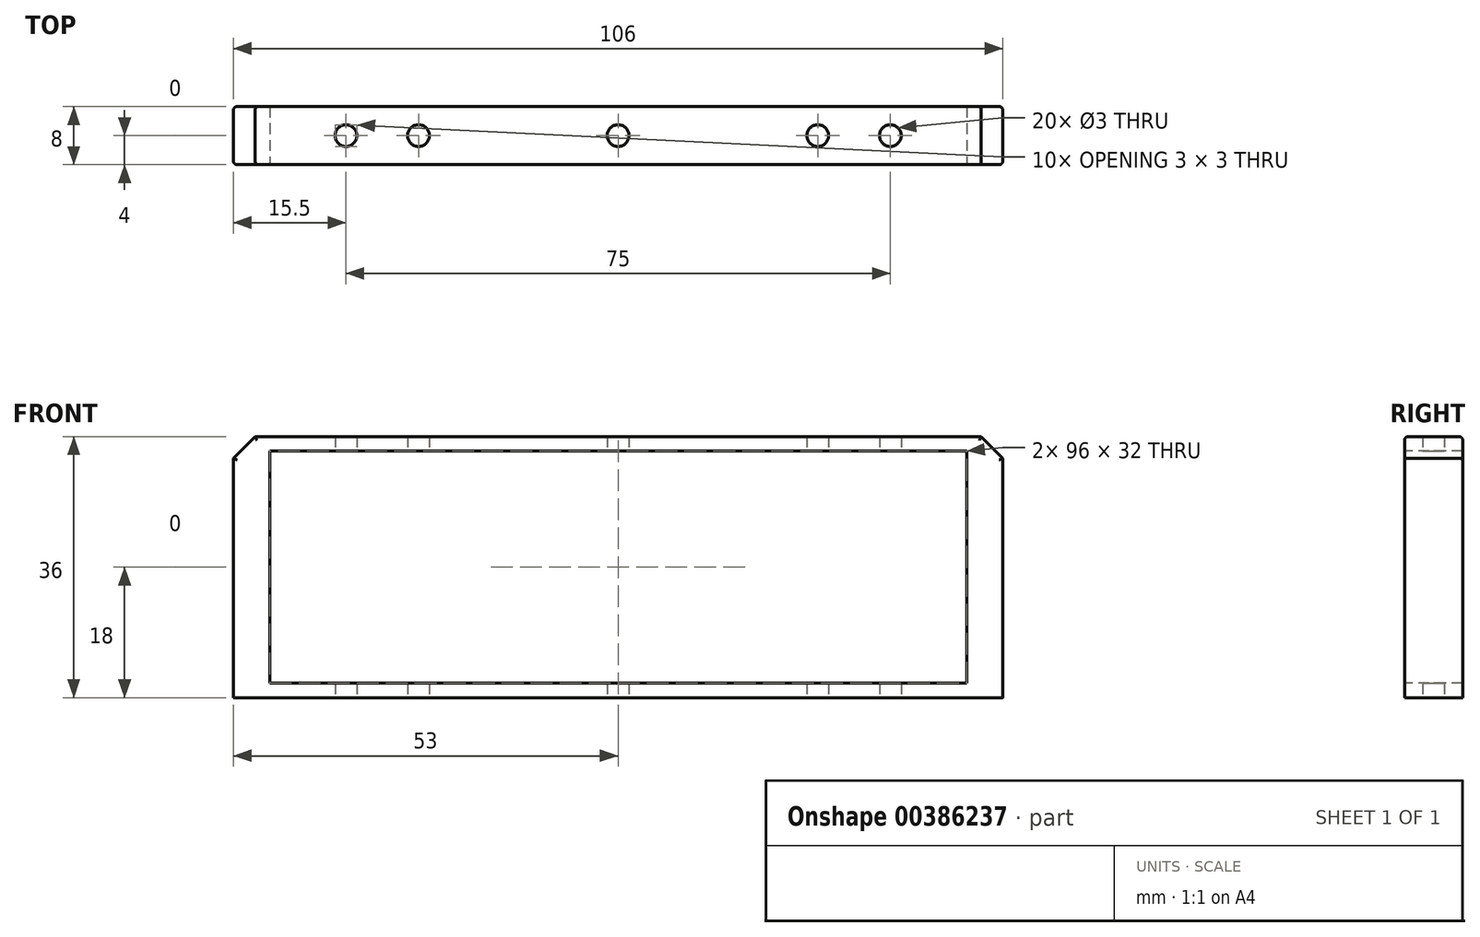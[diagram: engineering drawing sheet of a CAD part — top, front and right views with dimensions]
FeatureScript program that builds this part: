
annotation { "Feature Type Name" : "Feature", "Feature Type Description" : "" }
export const myFeature = defineFeature(function(context is Context, id is Id, definition is map)
    precondition{}
    {
        {
            assignVariable(context, id + "F0", {"name" : "height", "anyValue" : 36});
        }
        {
            var Q0;
            Q0=qCreatedBy(makeId("Top.planeOp"),FACE);
            var sketch = newSketch(context, id + "F1", { "sketchPlane" : qUnion([Q0])});
            skCircle(sketch, "E0", {"center": v(0, 0) * mm, "radius": 1.5 * mm});
            skCircle(sketch, "E1", {"center": v(37.5, 0) * mm, "radius": 1.5 * mm});
            skCircle(sketch, "E2", {"center": v(-37.5, 0) * mm, "radius": 1.5 * mm});
            skCircle(sketch, "E3", {"center": v(-27.5, 0) * mm, "radius": 1.5 * mm});
            skCircle(sketch, "E4", {"center": v(27.5, 0) * mm, "radius": 1.5 * mm});
            skLineSegment(sketch, "E5.bottom", {"start": v(-53, 4) * mm, "end": v(53, 4) * mm});
            skLineSegment(sketch, "E5.top", {"start": v(-53, -4) * mm, "end": v(53, -4) * mm});
            skLineSegment(sketch, "E5.left", {"start": v(-53, 4) * mm, "end": v(-53, -4) * mm});
            skLineSegment(sketch, "E5.right", {"start": v(53, 4) * mm, "end": v(53, -4) * mm});
            skSolve(sketch);
        }
        {
            var Q0;
            Q0=makeQuery(id+"F1.imprint","IMPRINT",FACE,{"disambiguationData":[TD([[makeQuery(id+"F1.imprint","IMPRINT",EDGE,{"derivedFrom":sQuery(id+"F1.wireOp",EDGE,"E0")}),-1.0]])]});
            var Q1;
            {var subQ0=sQuery(id+"F1.wireOp",EDGE,"E5.left");Q1=makeQuery(id+"F1.imprint","IMPRINT",FACE,{"disambiguationData":[TD([[makeQuery(id+"F1.imprint","IMPRINT",EDGE,{"derivedFrom":subQ0}),1.0]])]});}
            var Q2;
            {var subQ0=sQuery(id+"F1.wireOp",EDGE,"E5.right");Q2=makeQuery(id+"F1.imprint","IMPRINT",FACE,{"disambiguationData":[TD([[makeQuery(id+"F1.imprint","IMPRINT",EDGE,{"derivedFrom":subQ0}),-1.0]])]});}
            extrude(context, id + "F2", {"entities" : qUnion([Q0, Q1, Q2]), "depth" : (getVariable(context, 'height')) * mm});
        }
        {
            var Q0;
            Q0=makeQuery(id+"F2.opExtrude","SWEPT_FACE",FACE,{"disambiguationData":[OSD([sQuery(id+"F1.wireOp",EDGE,"E5.top")])]});
            var sketch = newSketch(context, id + "F3", { "sketchPlane" : qUnion([Q0])});
            skLineSegment(sketch, "E6.bottom", {"start": v(-48, 2) * mm, "end": v(48, 2) * mm});
            skLineSegment(sketch, "E6.top", {"start": v(-48, 34) * mm, "end": v(48, 34) * mm});
            skLineSegment(sketch, "E6.left", {"start": v(-48, 2) * mm, "end": v(-48, 34) * mm});
            skLineSegment(sketch, "E6.right", {"start": v(48, 2) * mm, "end": v(48, 34) * mm});
            skSolve(sketch);
        }
        {
            var Q0;
            Q0=makeQuery(id+"F3.imprint","IMPRINT",FACE,{"disambiguationData":[TD([[makeQuery(id+"F3.imprint","IMPRINT",EDGE,{"derivedFrom":sQuery(id+"F3.wireOp",EDGE,"E6.bottom")}),1.0]])]});
            extrude(context, id + "F4", {"entities" : qUnion([Q0]), "operationType" : NewBodyOperationType.REMOVE, "oppositeDirection" : true, "depth" : 25 * mm});
        }
        {
            var Q0;
            Q0=makeQuery(id+"F2.opExtrude","CAP_EDGE",EDGE,{"disambiguationData":[OSD([sQuery(id+"F1.wireOp",EDGE,"E5.left")])],"isStart":false});
            var Q1;
            Q1=makeQuery(id+"F2.opExtrude","CAP_EDGE",EDGE,{"disambiguationData":[OSD([sQuery(id+"F1.wireOp",EDGE,"E5.right")])],"isStart":false});
            chamfer(context, id + "F5", {"entities" : qUnion([Q0, Q1]), "width" : 3 * mm, "tangentPropagation" : true});
        }
        {
            var Q0;
            Q0=makeQuery(id+"F2.opExtrude","CAP_EDGE",EDGE,{"disambiguationData":[OSD([sQuery(id+"F1.wireOp",EDGE,"E5.top")])],"isStart":false});
            var Q1;
            Q1=makeQuery(id+"F2.opExtrude","CAP_EDGE",EDGE,{"disambiguationData":[OSD([sQuery(id+"F1.wireOp",EDGE,"E5.bottom")])],"isStart":false});
            var Q2;
            Q2=makeQuery(id+"F5.opChamfer","BLEND_EDGE",EDGE,{"blendedFrom":[makeQuery(id+"F2.opExtrude","CAP_EDGE",EDGE,{"disambiguationData":[OSD([sQuery(id+"F1.wireOp",EDGE,"E5.right")])],"isStart":false}),makeQuery(id+"F2.opExtrude","SWEPT_FACE",FACE,{"disambiguationData":[OSD([sQuery(id+"F1.wireOp",EDGE,"E5.top")])]})],"blendedInto":[makeQuery(id+"F2.opExtrude","SWEPT_FACE",FACE,{"disambiguationData":[OSD([sQuery(id+"F1.wireOp",EDGE,"E5.top")])]})]});
            var Q3;
            Q3=makeQuery(id+"F2.opExtrude","SWEPT_EDGE",EDGE,{"disambiguationData":[OSD([sQuery(id+"F1.wireOp",EDGE,"E5.top"),sQuery(id+"F1.wireOp",EDGE,"E5.right")])]});
            var Q4;
            Q4=makeQuery(id+"F5.opChamfer","BLEND_EDGE",EDGE,{"blendedFrom":[makeQuery(id+"F2.opExtrude","CAP_EDGE",EDGE,{"disambiguationData":[OSD([sQuery(id+"F1.wireOp",EDGE,"E5.right")])],"isStart":false}),makeQuery(id+"F2.opExtrude","SWEPT_FACE",FACE,{"disambiguationData":[OSD([sQuery(id+"F1.wireOp",EDGE,"E5.bottom")])]})],"blendedInto":[makeQuery(id+"F2.opExtrude","SWEPT_FACE",FACE,{"disambiguationData":[OSD([sQuery(id+"F1.wireOp",EDGE,"E5.bottom")])]})]});
            var Q5;
            Q5=makeQuery(id+"F2.opExtrude","SWEPT_EDGE",EDGE,{"disambiguationData":[OSD([sQuery(id+"F1.wireOp",EDGE,"E5.bottom"),sQuery(id+"F1.wireOp",EDGE,"E5.right")])]});
            var Q6;
            Q6=makeQuery(id+"F5.opChamfer","BLEND_EDGE",EDGE,{"blendedFrom":[makeQuery(id+"F2.opExtrude","CAP_EDGE",EDGE,{"disambiguationData":[OSD([sQuery(id+"F1.wireOp",EDGE,"E5.left")])],"isStart":false}),makeQuery(id+"F2.opExtrude","SWEPT_FACE",FACE,{"disambiguationData":[OSD([sQuery(id+"F1.wireOp",EDGE,"E5.top")])]})],"blendedInto":[makeQuery(id+"F2.opExtrude","SWEPT_FACE",FACE,{"disambiguationData":[OSD([sQuery(id+"F1.wireOp",EDGE,"E5.top")])]})]});
            var Q7;
            Q7=makeQuery(id+"F5.opChamfer","BLEND_EDGE",EDGE,{"blendedFrom":[makeQuery(id+"F2.opExtrude","CAP_EDGE",EDGE,{"disambiguationData":[OSD([sQuery(id+"F1.wireOp",EDGE,"E5.left")])],"isStart":false}),makeQuery(id+"F2.opExtrude","SWEPT_FACE",FACE,{"disambiguationData":[OSD([sQuery(id+"F1.wireOp",EDGE,"E5.bottom")])]})],"blendedInto":[makeQuery(id+"F2.opExtrude","SWEPT_FACE",FACE,{"disambiguationData":[OSD([sQuery(id+"F1.wireOp",EDGE,"E5.bottom")])]})]});
            var Q8;
            Q8=makeQuery(id+"F2.opExtrude","SWEPT_EDGE",EDGE,{"disambiguationData":[OSD([sQuery(id+"F1.wireOp",EDGE,"E5.top"),sQuery(id+"F1.wireOp",EDGE,"E5.left")])]});
            var Q9;
            Q9=makeQuery(id+"F2.opExtrude","SWEPT_EDGE",EDGE,{"disambiguationData":[OSD([sQuery(id+"F1.wireOp",EDGE,"E5.bottom"),sQuery(id+"F1.wireOp",EDGE,"E5.left")])]});
            fillet(context, id + "F6", {"entities" : qUnion([Q0, Q1, Q2, Q3, Q4, Q5, Q6, Q7, Q8, Q9]), "radius" : 0.5 * mm, "tangentPropagation" : true, "allowEdgeOverflow" : false});
        }
        {
            var Q0;
            Q0=makeQuery(id+"F2.opExtrude","SWEPT_BODY",BODY,{"disambiguationData":[OSD([sQuery(id+"F1.wireOp",EDGE,"E0"),sQuery(id+"F1.wireOp",EDGE,"E1"),sQuery(id+"F1.wireOp",EDGE,"E2"),sQuery(id+"F1.wireOp",EDGE,"E3"),sQuery(id+"F1.wireOp",EDGE,"E4"),sQuery(id+"F1.wireOp",EDGE,"E5.bottom"),sQuery(id+"F1.wireOp",EDGE,"E5.top"),sQuery(id+"F1.wireOp",EDGE,"E5.left"),sQuery(id+"F1.wireOp",EDGE,"E5.right")])]});
            transform(context, id + "F7", {"entities" : qUnion([Q0]), "transformType" : TransformType.TRANSLATION_3D, "dx" : 0 * mm, "dy" : 0 * mm, "dz" : 0 * mm, "makeCopy" : true});
        }
    });
